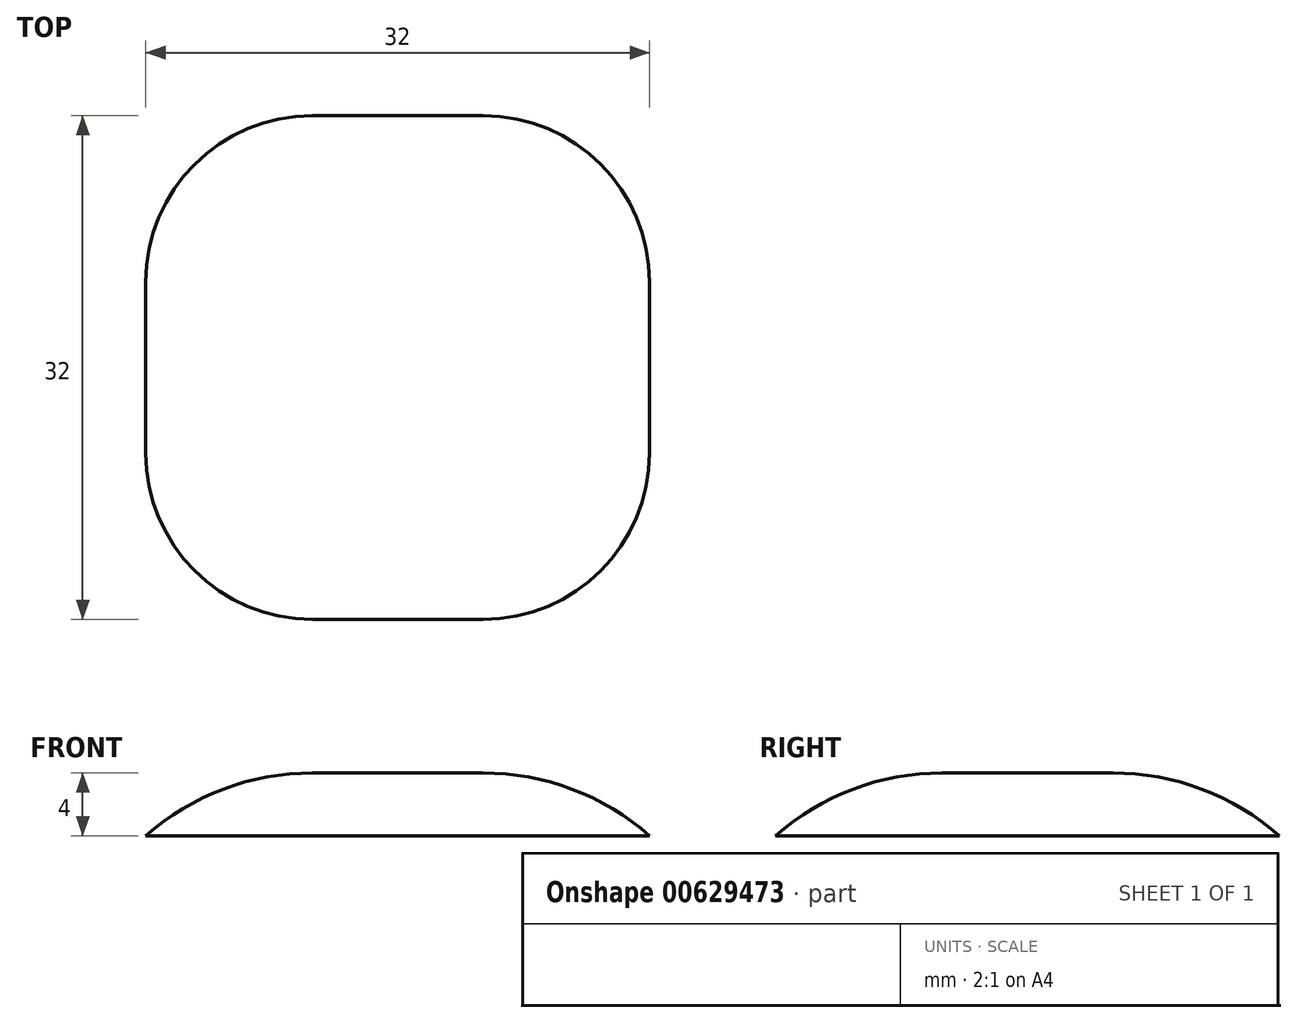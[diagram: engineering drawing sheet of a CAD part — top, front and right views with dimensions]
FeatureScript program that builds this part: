
annotation { "Feature Type Name" : "Feature", "Feature Type Description" : "" }
export const myFeature = defineFeature(function(context is Context, id is Id, definition is map)
    precondition{}
    {
        {
            var Q0;
            Q0=qCreatedBy(makeId("Top.planeOp"),FACE);
            var sketch = newSketch(context, id + "F0", { "sketchPlane" : qUnion([Q0])});
            skLineSegment(sketch, "E0.bottom", {"start": v(-16, 16) * mm, "end": v(16, 16) * mm});
            skLineSegment(sketch, "E0.top", {"start": v(-16, -16) * mm, "end": v(16, -16) * mm});
            skLineSegment(sketch, "E0.left", {"start": v(-16, 16) * mm, "end": v(-16, -16) * mm});
            skLineSegment(sketch, "E0.right", {"start": v(16, 16) * mm, "end": v(16, -16) * mm});
            skCircle(sketch, "E1", {"center": v(0, 8) * mm, "radius": 1.75 * mm});
            skCircle(sketch, "E2.1.0", {"center": v(-8, 0) * mm, "radius": 1.75 * mm});
            skCircle(sketch, "E2.2.0", {"center": v(0, -8) * mm, "radius": 1.75 * mm});
            skCircle(sketch, "E2.3.0", {"center": v(8, 0) * mm, "radius": 1.75 * mm});
            skPoint(sketch, "E2.center", {"position": v(0, 0) * mm});
            skSolve(sketch);
        }
        {
            var Q0;
            Q0=makeQuery(id+"F0.imprint","IMPRINT",FACE,{"disambiguationData":[TD([[makeQuery(id+"F0.imprint","IMPRINT",EDGE,{"derivedFrom":sQuery(id+"F0.wireOp",EDGE,"E0.bottom")}),-1.0]])]});
            var Q1;
            Q1=makeQuery(id+"F0.imprint","IMPRINT",FACE,{"disambiguationData":[TD([[makeQuery(id+"F0.imprint","IMPRINT",EDGE,{"derivedFrom":sQuery(id+"F0.wireOp",EDGE,"E2.1.0")}),1.0]])]});
            var Q2;
            Q2=makeQuery(id+"F0.imprint","IMPRINT",FACE,{"disambiguationData":[TD([[makeQuery(id+"F0.imprint","IMPRINT",EDGE,{"derivedFrom":sQuery(id+"F0.wireOp",EDGE,"E1")}),1.0]])]});
            var Q3;
            Q3=makeQuery(id+"F0.imprint","IMPRINT",FACE,{"disambiguationData":[TD([[makeQuery(id+"F0.imprint","IMPRINT",EDGE,{"derivedFrom":sQuery(id+"F0.wireOp",EDGE,"E2.3.0")}),1.0]])]});
            var Q4;
            Q4=makeQuery(id+"F0.imprint","IMPRINT",FACE,{"disambiguationData":[TD([[makeQuery(id+"F0.imprint","IMPRINT",EDGE,{"derivedFrom":sQuery(id+"F0.wireOp",EDGE,"E2.2.0")}),1.0]])]});
            extrude(context, id + "F1", {"entities" : qUnion([Q0, Q1, Q2, Q3, Q4]), "depth" : 4 * mm, "offsetDistance" : 25 * mm});
        }
        {
            var Q0;
            Q0=makeQuery(id+"F1.opExtrude","CAP_EDGE",EDGE,{"disambiguationData":[OSD([sQuery(id+"F0.wireOp",EDGE,"E0.bottom")])],"isStart":false});
            var Q1;
            Q1=makeQuery(id+"F1.opExtrude","CAP_EDGE",EDGE,{"disambiguationData":[OSD([sQuery(id+"F0.wireOp",EDGE,"E0.left")])],"isStart":false});
            var Q2;
            Q2=makeQuery(id+"F1.opExtrude","CAP_EDGE",EDGE,{"disambiguationData":[OSD([sQuery(id+"F0.wireOp",EDGE,"E0.top")])],"isStart":false});
            var Q3;
            Q3=makeQuery(id+"F1.opExtrude","CAP_EDGE",EDGE,{"disambiguationData":[OSD([sQuery(id+"F0.wireOp",EDGE,"E0.right")])],"isStart":false});
            fillet(context, id + "F2", {"entities" : qUnion([Q0, Q1, Q2, Q3]), "radius" : 16 * mm, "tangentPropagation" : true, "allowEdgeOverflow" : false});
        }
        {
            var Q0;
            Q0=makeQuery(id+"F2.opFillet","BLEND_EDGE",EDGE,{"blendedFrom":[makeQuery(id+"F1.opExtrude","CAP_EDGE",EDGE,{"disambiguationData":[OSD([sQuery(id+"F0.wireOp",EDGE,"E0.bottom")])],"isStart":false}),makeQuery(id+"F1.opExtrude","CAP_EDGE",EDGE,{"disambiguationData":[OSD([sQuery(id+"F0.wireOp",EDGE,"E0.left")])],"isStart":false})],"blendedInto":[]});
            var Q1;
            Q1=makeQuery(id+"F2.opFillet","BLEND_EDGE",EDGE,{"blendedFrom":[makeQuery(id+"F1.opExtrude","CAP_EDGE",EDGE,{"disambiguationData":[OSD([sQuery(id+"F0.wireOp",EDGE,"E0.bottom")])],"isStart":false}),makeQuery(id+"F1.opExtrude","CAP_EDGE",EDGE,{"disambiguationData":[OSD([sQuery(id+"F0.wireOp",EDGE,"E0.right")])],"isStart":false})],"blendedInto":[]});
            var Q2;
            Q2=makeQuery(id+"F2.opFillet","BLEND_EDGE",EDGE,{"blendedFrom":[makeQuery(id+"F1.opExtrude","CAP_EDGE",EDGE,{"disambiguationData":[OSD([sQuery(id+"F0.wireOp",EDGE,"E0.top")])],"isStart":false}),makeQuery(id+"F1.opExtrude","CAP_EDGE",EDGE,{"disambiguationData":[OSD([sQuery(id+"F0.wireOp",EDGE,"E0.right")])],"isStart":false})],"blendedInto":[]});
            var Q3;
            Q3=makeQuery(id+"F2.opFillet","BLEND_EDGE",EDGE,{"blendedFrom":[makeQuery(id+"F1.opExtrude","CAP_EDGE",EDGE,{"disambiguationData":[OSD([sQuery(id+"F0.wireOp",EDGE,"E0.top")])],"isStart":false}),makeQuery(id+"F1.opExtrude","CAP_EDGE",EDGE,{"disambiguationData":[OSD([sQuery(id+"F0.wireOp",EDGE,"E0.left")])],"isStart":false})],"blendedInto":[]});
            fillet(context, id + "F3", {"entities" : qUnion([Q0, Q1, Q2, Q3]), "radius" : 16 * mm, "tangentPropagation" : true, "allowEdgeOverflow" : false});
        }
    });
